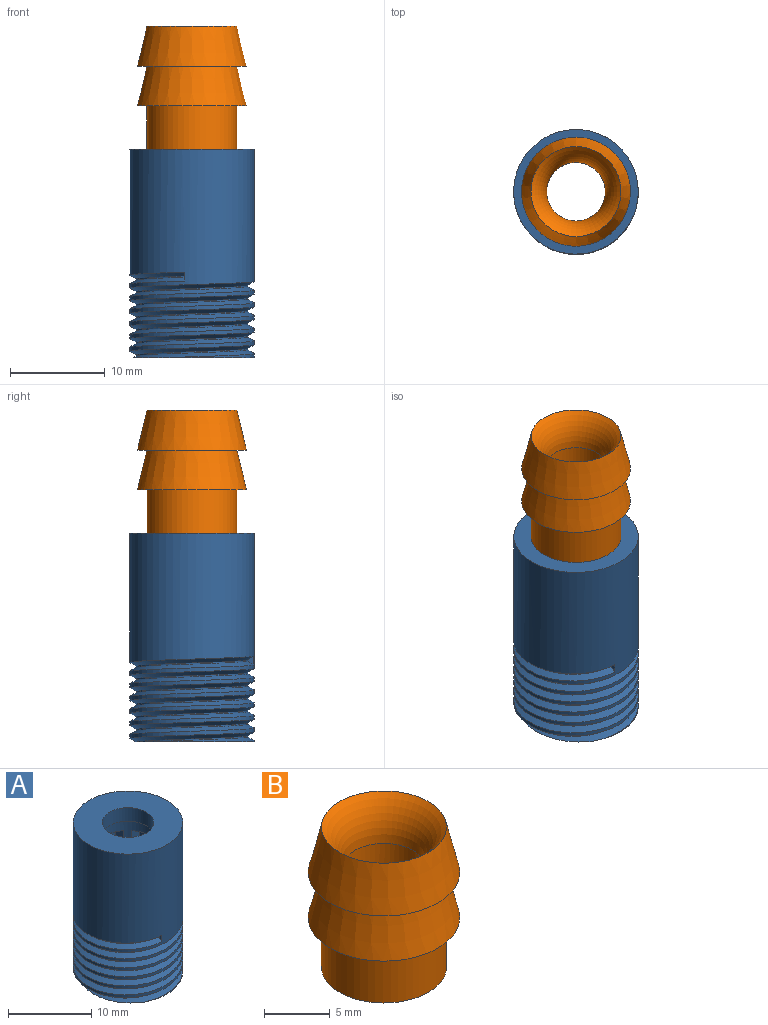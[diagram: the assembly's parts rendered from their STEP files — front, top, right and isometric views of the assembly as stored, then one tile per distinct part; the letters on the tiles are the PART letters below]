
ASSEMBLY  parts=2 mates=1
PART A: 37 faces, bbox 13.2x13.2x22.4 mm
  f0: cylinder r=6.58mm len=9.61mm, axis (0,0,-1), area 2.9mm2, adj f1,f9,f34,f35
  f1: cylinder r=6.58mm len=13.16mm, axis (0,0,-1), area 16.5mm2, adj f0,f2,f33,f34
  f2: cylinder r=6.58mm len=13.16mm, axis (0,0,-1), area 16.5mm2, adj f1,f3,f33,f34
  f3: cylinder r=6.58mm len=13.16mm, axis (0,0,-1), area 16.5mm2, adj f2,f4,f33,f34
  f4: cylinder r=6.58mm len=13.16mm, axis (0,0,-1), area 16.5mm2, adj f3,f5,f33,f34
  f5: cylinder r=6.58mm len=13.16mm, axis (0,0,-1), area 16.5mm2, adj f4,f6,f33,f34
  f6: cylinder r=6.58mm len=15.28mm, axis (0,0,-1), area 575.5mm2, adj f5,f7,f33,f34,f36
  f7: plane 13.16x13.16mm, normal (0,0,1), area 105.8mm2, adj f6,f8
  f8: cylinder r=3.1mm len=6.2mm, axis (0,0,1), area 39mm2, adj f7,f11
  f9: plane 12.78x12.54mm, normal (0,0,-1), area 49.3mm2, adj f0,f10,f13,f14,f15,f17,f18,f19
  f10: cylinder r=4mm len=20mm, axis (0,0,-1), area 139.8mm2, adj f9,f11,f12,f13,f14,f16,f17,f18
  f11: plane 8x8mm, normal (0,0,-1), area 20.1mm2, adj f8,f10
  f12: plane 4.07x2.21mm, normal (0,0,-1), area 5.1mm2, adj f10,f13,f14,f15
  f13: plane 18x1.64mm, normal (0.99,-0.15,0), area 29.8mm2, adj f9,f10,f12,f15
  f14: plane 18x1.64mm, normal (-0.99,0.15,0), area 29.8mm2, adj f9,f10,f12,f15
  f15: plane 18x3.82mm, normal (-0.15,-0.99,0), area 69.5mm2, adj f9,f12,f13,f14
  f16: plane 4.2x3.21mm, normal (0,0,-1), area 5.1mm2, adj f10,f17,f18,f19
  f17: plane 18x1.48mm, normal (-0.45,-0.89,0), area 29.8mm2, adj f9,f10,f16,f19
  f18: plane 18x1.48mm, normal (0.45,0.89,0), area 29.8mm2, adj f9,f10,f16,f19
  f19: plane 18x3.46mm, normal (0.89,-0.45,0), area 69.5mm2, adj f9,f16,f17,f18
  f20: plane 3.91x3.89mm, normal (0,0,-1), area 5.1mm2, adj f10,f21,f22,f23
  f21: plane 18x1.18mm, normal (-0.71,0.7,0), area 29.8mm2, adj f9,f10,f20,f23
  f22: plane 18x1.18mm, normal (0.71,-0.7,0), area 29.8mm2, adj f9,f10,f20,f23
  f23: plane 18x2.75mm, normal (0.7,0.71,0), area 69.5mm2, adj f9,f20,f21,f22
  f24: plane 4.19x3.25mm, normal (0,0,-1), area 5.1mm2, adj f10,f25,f26,f27
  f25: plane 18x1.47mm, normal (-0.89,-0.46,0), area 29.8mm2, adj f9,f10,f24,f27
  f26: plane 18x1.47mm, normal (0.89,0.46,0), area 29.8mm2, adj f9,f10,f24,f27
  f27: plane 18x3.43mm, normal (-0.46,0.89,0), area 69.5mm2, adj f9,f24,f25,f26
  f28: plane 4.08x2.27mm, normal (0,0,-1), area 5.1mm2, adj f10,f29,f30,f31
  f29: plane 18x1.63mm, normal (-0.16,0.99,0), area 29.8mm2, adj f9,f10,f28,f30
  f30: plane 18x3.81mm, normal (-0.99,-0.16,0), area 69.5mm2, adj f9,f28,f29,f31
  f31: plane 18x1.63mm, normal (0.16,-0.99,0), area 29.8mm2, adj f9,f10,f28,f30
  f32: cylinder r=5.9mm len=11.8mm, axis (0,0,-1), area 32.7mm2, adj f9,f33,f34,f36
  f33: bspline ~13.15x13.15mm, area 202.4mm2, adj f1,f2,f3,f4,f5,f6,f9,f32
  f34: bspline ~13.14x13.12mm, area 190mm2, adj f0,f1,f2,f3,f4,f5,f6,f9
  f35: plane 0.07x0.04mm, normal (0,1,0), area 0mm2, adj f0,f9,f33
  f36: plane 0.94x0.67mm, normal (-0.99,0.12,0), area 0.4mm2, adj f6,f32,f33,f34
PART B: 8 faces, bbox 17.5x17.5x14.3 mm
  f0: cylinder r=3.1mm len=9.29mm, axis (0,0,1), area 180.9mm2, adj f6,f7
  f1: cylinder r=4.75mm len=9.5mm, axis (0,0,-1), area 137.3mm2, adj f2,f7
  f2: plane 11.5x11.5mm, normal (0,0,-1), area 33mm2, adj f1,f3
  f3: cone r=4.75mm half-angle=13.4deg, axis (0,0,-1), area 142.4mm2, adj f2,f4
  f4: plane 11.5x11.5mm, normal (0,0,-1), area 33mm2, adj f3,f5
  f5: cone r=4.75mm half-angle=13.4deg, axis (0,0,-1), area 142.4mm2, adj f4,f6
  f6: torus R=8.1mm, axis (0,0,1), area 96.3mm2, adj f0,f5
  f7: plane 9.5x9.5mm, normal (0,0,-1), area 40.7mm2, adj f0,f1
PLACE A t=(-14.2,18.72,-16.19)mm
PLACE B t=(-14.2,18.72,-19.19)mm
MATE planar B.f6 <-> A.f0  axis (0,0,-1) through (-14.2,18.72,5.81)mm
